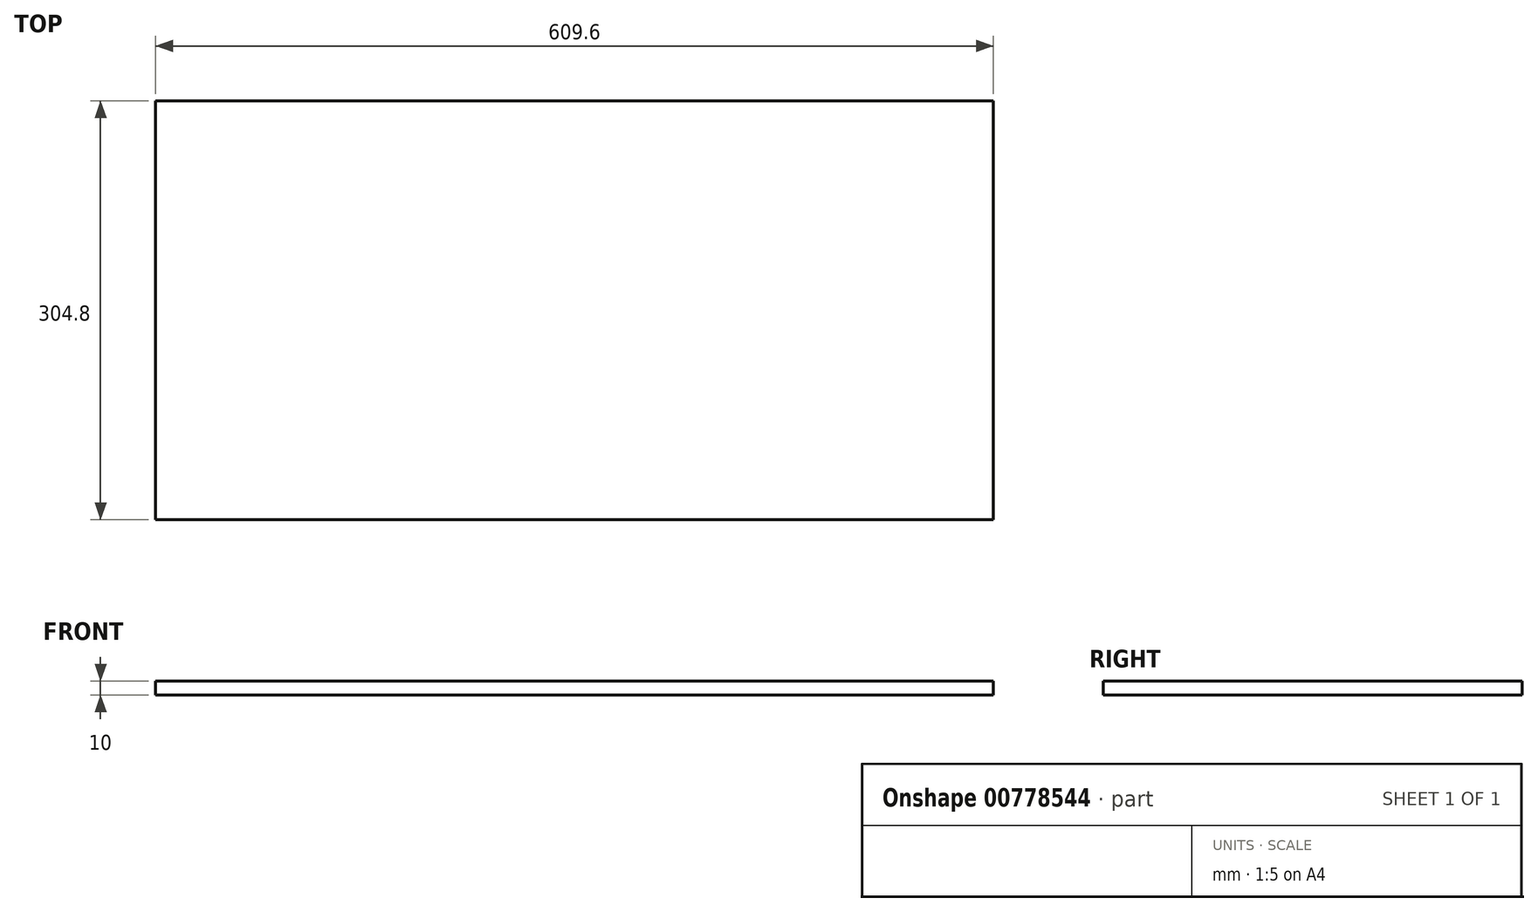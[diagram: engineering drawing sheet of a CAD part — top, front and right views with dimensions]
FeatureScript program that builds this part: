
annotation { "Feature Type Name" : "Feature", "Feature Type Description" : "" }
export const myFeature = defineFeature(function(context is Context, id is Id, definition is map)
    precondition{}
    {
        {
            var Q0;
            Q0=qCreatedBy(makeId("Top.planeOp"),FACE);
            var sketch = newSketch(context, id + "F0", { "sketchPlane" : qUnion([Q0])});
            skLineSegment(sketch, "E0.bottom", {"start": v(-306.46, 83.95) * mm, "end": v(303.14, 83.95) * mm});
            skLineSegment(sketch, "E0.top", {"start": v(-306.46, -220.85) * mm, "end": v(303.14, -220.85) * mm});
            skLineSegment(sketch, "E0.left", {"start": v(-306.46, 83.95) * mm, "end": v(-306.46, -220.85) * mm});
            skLineSegment(sketch, "E0.right", {"start": v(303.14, 83.95) * mm, "end": v(303.14, -220.85) * mm});
            skSolve(sketch);
        }
        {
            var Q0;
            Q0=makeQuery(id+"F0.imprint","IMPRINT",FACE,{"disambiguationData":[TD([[makeQuery(id+"F0.imprint","IMPRINT",EDGE,{"derivedFrom":sQuery(id+"F0.wireOp",EDGE,"E0.bottom")}),-1.0]])]});
            extrude(context, id + "F1", {"entities" : qUnion([Q0]), "depth" : 10 * mm, "offsetDistance" : 25.4 * mm});
        }
    });
